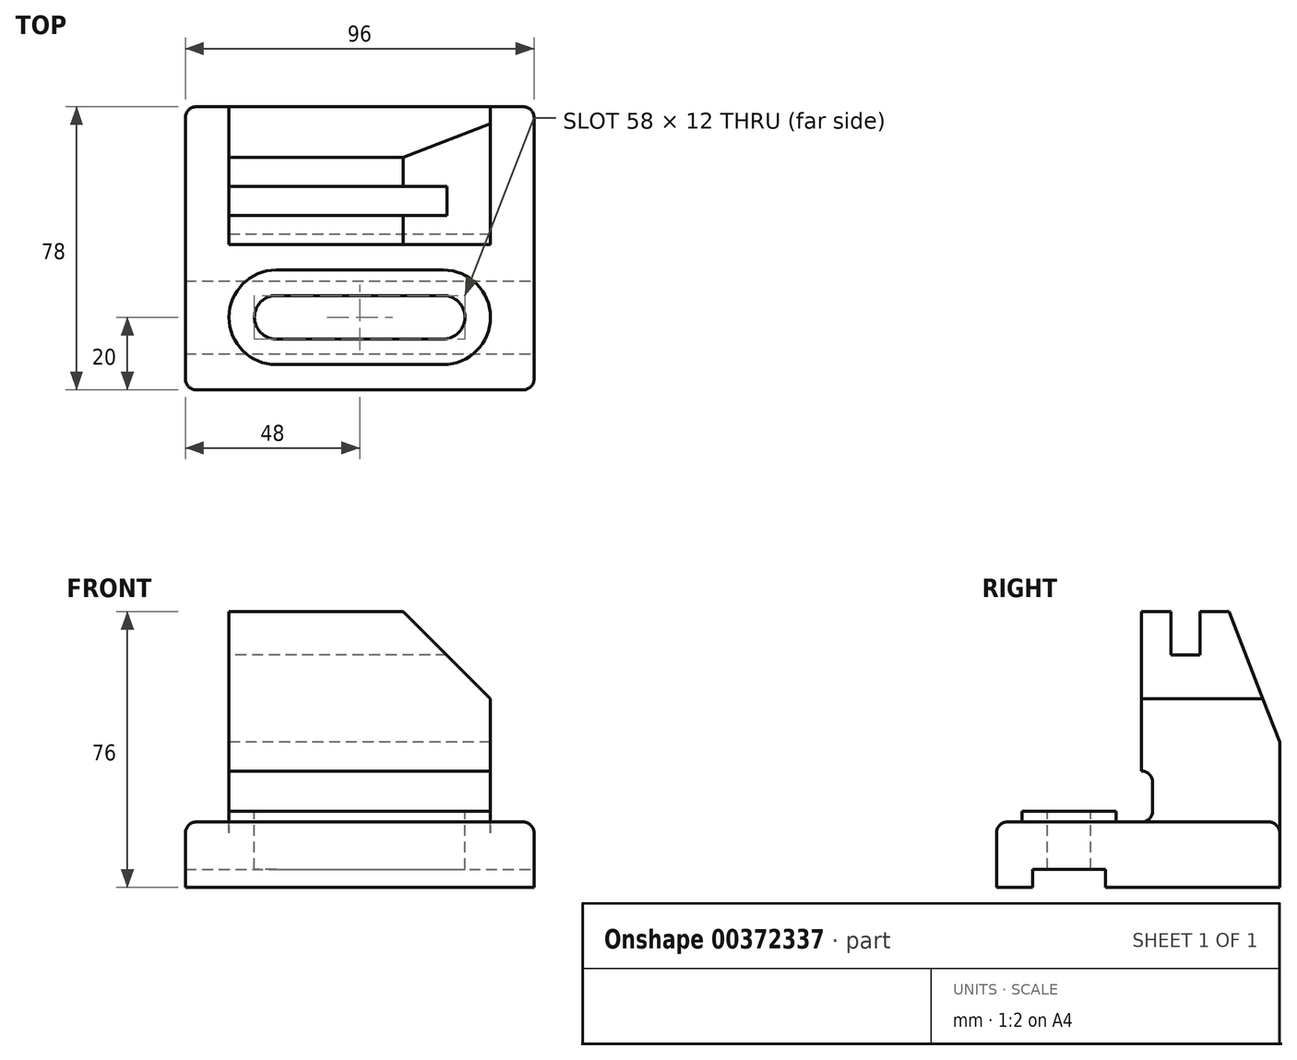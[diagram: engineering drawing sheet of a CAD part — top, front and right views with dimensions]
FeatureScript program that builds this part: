
annotation { "Feature Type Name" : "Feature", "Feature Type Description" : "" }
export const myFeature = defineFeature(function(context is Context, id is Id, definition is map)
    precondition{}
    {
        {
            var Q0;
            Q0=qCreatedBy(makeId("Top.planeOp"),FACE);
            var sketch = newSketch(context, id + "F0", { "sketchPlane" : qUnion([Q0])});
            skLineSegment(sketch, "E0.bottom", {"start": v(0, 0) * mm, "end": v(96, 0) * mm});
            skLineSegment(sketch, "E0.top", {"start": v(0, 78) * mm, "end": v(96, 78) * mm});
            skLineSegment(sketch, "E0.left", {"start": v(0, 0) * mm, "end": v(0, 78) * mm});
            skLineSegment(sketch, "E0.right", {"start": v(96, 0) * mm, "end": v(96, 78) * mm});
            skSolve(sketch);
        }
        {
            var Q0;
            Q0=makeQuery(id+"F0.imprint","IMPRINT",FACE,{"disambiguationData":[TD([[makeQuery(id+"F0.imprint","IMPRINT",EDGE,{"derivedFrom":sQuery(id+"F0.wireOp",EDGE,"E0.bottom")}),1.0]])]});
            extrude(context, id + "F1", {"entities" : qUnion([Q0]), "depth" : 18 * mm});
        }
        {
            var Q0;
            Q0=makeQuery(id+"F1.opExtrude","CAP_FACE",FACE,{"disambiguationData":[OSD([sQuery(id+"F0.wireOp",EDGE,"E0.bottom"),sQuery(id+"F0.wireOp",EDGE,"E0.top"),sQuery(id+"F0.wireOp",EDGE,"E0.left"),sQuery(id+"F0.wireOp",EDGE,"E0.right")])],"isStart":false});
            var sketch = newSketch(context, id + "F2", { "sketchPlane" : qUnion([Q0])});
            skLineSegment(sketch, "E1.bottom", {"start": v(12, 78) * mm, "end": v(84, 78) * mm});
            skLineSegment(sketch, "E1.top", {"start": v(12, 40) * mm, "end": v(84, 40) * mm});
            skLineSegment(sketch, "E1.left", {"start": v(12, 78) * mm, "end": v(12, 40) * mm});
            skLineSegment(sketch, "E1.right", {"start": v(84, 78) * mm, "end": v(84, 40) * mm});
            skSolve(sketch);
        }
        {
            var Q0;
            Q0=makeQuery(id+"F1.opExtrude","CAP_FACE",FACE,{"disambiguationData":[OSD([sQuery(id+"F0.wireOp",EDGE,"E0.bottom"),sQuery(id+"F0.wireOp",EDGE,"E0.top"),sQuery(id+"F0.wireOp",EDGE,"E0.left"),sQuery(id+"F0.wireOp",EDGE,"E0.right")])],"isStart":true});
            cPlane(context, id + "F3", {"entities" : qUnion([Q0]), "cplaneType" : CPlaneType.OFFSET, "offset" : 76 * mm, "oppositeDirection" : true, "width" : 150 * mm, "height" : 150 * mm});
        }
        {
            var Q0;
            Q0 = qSketchRegion(id + "F2", true);
            var Q1;
            Q1=qCreatedBy(id+"F3.planeOp",FACE);
            extrude(context, id + "F4", {"entities" : qUnion([Q0]), "operationType" : NewBodyOperationType.ADD, "endBound" : BoundingType.UP_TO_SURFACE, "endBoundEntityFace" : qUnion([Q1]), "depth" : 25 * mm});
        }
        {
            var Q0;
            Q0=makeQuery(id+"F4.opExtrude","SWEPT_FACE",FACE,{"disambiguationData":[OSD([sQuery(id+"F2.wireOp",EDGE,"E1.top")])]});
            var sketch = newSketch(context, id + "F5", { "sketchPlane" : qUnion([Q0])});
            skLineSegment(sketch, "E2", {"start": v(60, 76) * mm, "end": v(84, 76) * mm});
            skLineSegment(sketch, "E3", {"start": v(84, 76) * mm, "end": v(84, 52) * mm});
            skLineSegment(sketch, "E4", {"start": v(84, 52) * mm, "end": v(60, 76) * mm});
            skSolve(sketch);
        }
        {
            var Q0;
            Q0 = qSketchRegion(id + "F5", true);
            extrude(context, id + "F6", {"entities" : qUnion([Q0]), "operationType" : NewBodyOperationType.REMOVE, "endBound" : BoundingType.UP_TO_NEXT, "oppositeDirection" : true, "depth" : 25 * mm});
        }
        {
            var Q0;
            Q0=makeQuery(id+"F4.opExtrude","SWEPT_FACE",FACE,{"disambiguationData":[OSD([sQuery(id+"F2.wireOp",EDGE,"E1.left")])]});
            var sketch = newSketch(context, id + "F7", { "sketchPlane" : qUnion([Q0])});
            skLineSegment(sketch, "E5", {"start": v(-78, 40) * mm, "end": v(-78, 76) * mm});
            skLineSegment(sketch, "E6", {"start": v(-78, 76) * mm, "end": v(-64, 76) * mm});
            skLineSegment(sketch, "E7", {"start": v(-64, 76) * mm, "end": v(-78, 40) * mm});
            skSolve(sketch);
        }
        {
            var Q0;
            Q0 = qSketchRegion(id + "F7", true);
            extrude(context, id + "F8", {"entities" : qUnion([Q0]), "operationType" : NewBodyOperationType.REMOVE, "endBound" : BoundingType.UP_TO_NEXT, "oppositeDirection" : true, "depth" : 25 * mm});
        }
        {
            var Q0;
            Q0=makeQuery(id+"F4.opExtrude","SWEPT_FACE",FACE,{"disambiguationData":[OSD([sQuery(id+"F2.wireOp",EDGE,"E1.left")])]});
            var sketch = newSketch(context, id + "F9", { "sketchPlane" : qUnion([Q0])});
            skLineSegment(sketch, "E8.bottom", {"start": v(-48, 76) * mm, "end": v(-56, 76) * mm});
            skLineSegment(sketch, "E8.top", {"start": v(-48, 64) * mm, "end": v(-56, 64) * mm});
            skLineSegment(sketch, "E8.left", {"start": v(-48, 76) * mm, "end": v(-48, 64) * mm});
            skLineSegment(sketch, "E8.right", {"start": v(-56, 76) * mm, "end": v(-56, 64) * mm});
            skSolve(sketch);
        }
        {
            var Q0;
            Q0 = qSketchRegion(id + "F9", true);
            extrude(context, id + "F10", {"entities" : qUnion([Q0]), "operationType" : NewBodyOperationType.REMOVE, "endBound" : BoundingType.UP_TO_NEXT, "oppositeDirection" : true, "depth" : 25 * mm});
        }
        {
            var Q0;
            Q0=makeQuery(id+"F1.opExtrude","CAP_FACE",FACE,{"disambiguationData":[OSD([sQuery(id+"F0.wireOp",EDGE,"E0.bottom"),sQuery(id+"F0.wireOp",EDGE,"E0.top"),sQuery(id+"F0.wireOp",EDGE,"E0.left"),sQuery(id+"F0.wireOp",EDGE,"E0.right")])],"isStart":false});
            var sketch = newSketch(context, id + "F11", { "sketchPlane" : qUnion([Q0])});
            skLineSegment(sketch, "E9", {"start": v(25, 33) * mm, "end": v(71, 33) * mm});
            skLineSegment(sketch, "E10", {"start": v(25, 7) * mm, "end": v(71, 7) * mm});
            skArc(sketch, "E11", {"start": v(25, 33) * mm, "mid": v(12, 20) * mm, "end": v(25, 7) * mm});
            skArc(sketch, "E12", {"start": v(71, 33) * mm, "mid": v(84, 20) * mm, "end": v(71, 7) * mm});
            skSolve(sketch);
        }
        {
            var Q0;
            Q0 = qSketchRegion(id + "F11", true);
            extrude(context, id + "F12", {"entities" : qUnion([Q0]), "operationType" : NewBodyOperationType.ADD, "depth" : 3 * mm});
        }
        {
            var Q0;
            Q0=makeQuery(id+"F12.opExtrude","CAP_FACE",FACE,{"disambiguationData":[OSD([sQuery(id+"F11.wireOp",EDGE,"E9"),sQuery(id+"F11.wireOp",EDGE,"E10"),sQuery(id+"F11.wireOp",EDGE,"E11"),sQuery(id+"F11.wireOp",EDGE,"E12")])],"isStart":false});
            var sketch = newSketch(context, id + "F13", { "sketchPlane" : qUnion([Q0])});
            skLineSegment(sketch, "E13", {"start": v(25, 26) * mm, "end": v(71, 26) * mm});
            skLineSegment(sketch, "E14", {"start": v(25, 14) * mm, "end": v(71, 14) * mm});
            skArc(sketch, "E15", {"start": v(25, 26) * mm, "mid": v(19, 20) * mm, "end": v(25, 14) * mm});
            skArc(sketch, "E16", {"start": v(71, 26) * mm, "mid": v(77, 20) * mm, "end": v(71, 14) * mm});
            skSolve(sketch);
        }
        {
            var Q0;
            Q0 = qSketchRegion(id + "F13", true);
            extrude(context, id + "F14", {"entities" : qUnion([Q0]), "operationType" : NewBodyOperationType.REMOVE, "endBound" : BoundingType.UP_TO_NEXT, "oppositeDirection" : true, "depth" : 25 * mm});
        }
        {
            var Q0;
            Q0=makeQuery(id+"F1.opExtrude","SWEPT_FACE",FACE,{"disambiguationData":[OSD([sQuery(id+"F0.wireOp",EDGE,"E0.right")])]});
            var sketch = newSketch(context, id + "F15", { "sketchPlane" : qUnion([Q0])});
            skLineSegment(sketch, "E17.bottom", {"start": v(10, 0) * mm, "end": v(30, 0) * mm});
            skLineSegment(sketch, "E17.top", {"start": v(10, 5) * mm, "end": v(30, 5) * mm});
            skLineSegment(sketch, "E17.left", {"start": v(10, 0) * mm, "end": v(10, 5) * mm});
            skLineSegment(sketch, "E17.right", {"start": v(30, 0) * mm, "end": v(30, 5) * mm});
            skPoint(sketch, "E18", {"position": v(20, 5) * mm});
            skSolve(sketch);
        }
        {
            var Q0;
            Q0 = qSketchRegion(id + "F15", true);
            extrude(context, id + "F16", {"entities" : qUnion([Q0]), "operationType" : NewBodyOperationType.REMOVE, "endBound" : BoundingType.THROUGH_ALL, "oppositeDirection" : true, "depth" : 25 * mm});
        }
        {
            var Q0;
            Q0=makeQuery(id+"F4.opExtrude","SWEPT_FACE",FACE,{"disambiguationData":[OSD([sQuery(id+"F2.wireOp",EDGE,"E1.right")])]});
            var sketch = newSketch(context, id + "F17", { "sketchPlane" : qUnion([Q0])});
            skLineSegment(sketch, "E19.bottom", {"start": v(40, 32) * mm, "end": v(43, 32) * mm});
            skLineSegment(sketch, "E19.top", {"start": v(40, 18) * mm, "end": v(43, 18) * mm});
            skLineSegment(sketch, "E19.left", {"start": v(40, 32) * mm, "end": v(40, 18) * mm});
            skLineSegment(sketch, "E19.right", {"start": v(43, 32) * mm, "end": v(43, 18) * mm});
            skSolve(sketch);
        }
        {
            var Q0;
            Q0 = qSketchRegion(id + "F17", true);
            extrude(context, id + "F18", {"entities" : qUnion([Q0]), "operationType" : NewBodyOperationType.REMOVE, "endBound" : BoundingType.UP_TO_NEXT, "oppositeDirection" : true, "depth" : 25 * mm});
        }
        {
            var Q0;
            Q0=makeQuery(id+"F18.boolean.opBoolean","COPY",EDGE,{"derivedFrom":makeQuery(id+"F18.opExtrude","SWEPT_EDGE",EDGE,{"disambiguationData":[OSD([sQuery(id+"F2.wireOp",EDGE,"E1.right"),sQuery(id+"F17.wireOp",EDGE,"E19.top"),sQuery(id+"F17.wireOp",EDGE,"E19.right")])]})});
            var Q1;
            Q1=makeQuery(id+"F18.boolean.opBoolean","COPY",EDGE,{"derivedFrom":makeQuery(id+"F18.opExtrude","SWEPT_EDGE",EDGE,{"disambiguationData":[OSD([sQuery(id+"F17.wireOp",EDGE,"E19.bottom"),sQuery(id+"F17.wireOp",EDGE,"E19.right")])]})});
            var Q2;
            Q2=makeQuery(id+"F1.opExtrude","CAP_EDGE",EDGE,{"disambiguationData":[OSD([sQuery(id+"F0.wireOp",EDGE,"E0.right")])],"isStart":false});
            var Q3;
            Q3=makeQuery(id+"F1.opExtrude","CAP_EDGE",EDGE,{"disambiguationData":[OSD([sQuery(id+"F0.wireOp",EDGE,"E0.bottom")])],"isStart":false});
            var Q4;
            Q4=makeQuery(id+"F1.opExtrude","SWEPT_EDGE",EDGE,{"disambiguationData":[OSD([sQuery(id+"F0.wireOp",EDGE,"E0.bottom"),sQuery(id+"F0.wireOp",EDGE,"E0.right")])]});
            var Q5;
            Q5=makeQuery(id+"F1.opExtrude","SWEPT_EDGE",EDGE,{"disambiguationData":[OSD([sQuery(id+"F0.wireOp",EDGE,"E0.top"),sQuery(id+"F0.wireOp",EDGE,"E0.right")])]});
            var Q6;
            {var subQ0=sQuery(id+"F0.wireOp",EDGE,"E0.right");var subQ1=sQuery(id+"F0.wireOp",EDGE,"E0.top");Q6=makeQuery(id+"F4.boolean.opBoolean","SPLIT",EDGE,{"disambiguationData":[TD([makeQuery(id+"F1.opExtrude","SWEPT_FACE",FACE,{"disambiguationData":[OSD([subQ0])]})])],"derivedFrom":makeQuery(id+"F1.opExtrude","CAP_EDGE",EDGE,{"disambiguationData":[OSD([subQ1])],"isStart":false})});}
            var Q7;
            Q7=makeQuery(id+"F1.opExtrude","CAP_EDGE",EDGE,{"disambiguationData":[OSD([sQuery(id+"F0.wireOp",EDGE,"E0.left")])],"isStart":false});
            var Q8;
            Q8=makeQuery(id+"F1.opExtrude","SWEPT_EDGE",EDGE,{"disambiguationData":[OSD([sQuery(id+"F0.wireOp",EDGE,"E0.bottom"),sQuery(id+"F0.wireOp",EDGE,"E0.left")])]});
            var Q9;
            Q9=makeQuery(id+"F1.opExtrude","SWEPT_EDGE",EDGE,{"disambiguationData":[OSD([sQuery(id+"F0.wireOp",EDGE,"E0.top"),sQuery(id+"F0.wireOp",EDGE,"E0.left")])]});
            var Q10;
            {var subQ0=sQuery(id+"F0.wireOp",EDGE,"E0.left");var subQ1=sQuery(id+"F0.wireOp",EDGE,"E0.top");Q10=makeQuery(id+"F4.boolean.opBoolean","SPLIT",EDGE,{"disambiguationData":[TD([makeQuery(id+"F1.opExtrude","SWEPT_FACE",FACE,{"disambiguationData":[OSD([subQ0])]})])],"derivedFrom":makeQuery(id+"F1.opExtrude","CAP_EDGE",EDGE,{"disambiguationData":[OSD([subQ1])],"isStart":false})});}
            fillet(context, id + "F19", {"entities" : qUnion([Q0, Q1, Q2, Q3, Q4, Q5, Q6, Q7, Q8, Q9, Q10]), "radius" : 3 * mm, "tangentPropagation" : true, "allowEdgeOverflow" : false});
        }
    });
